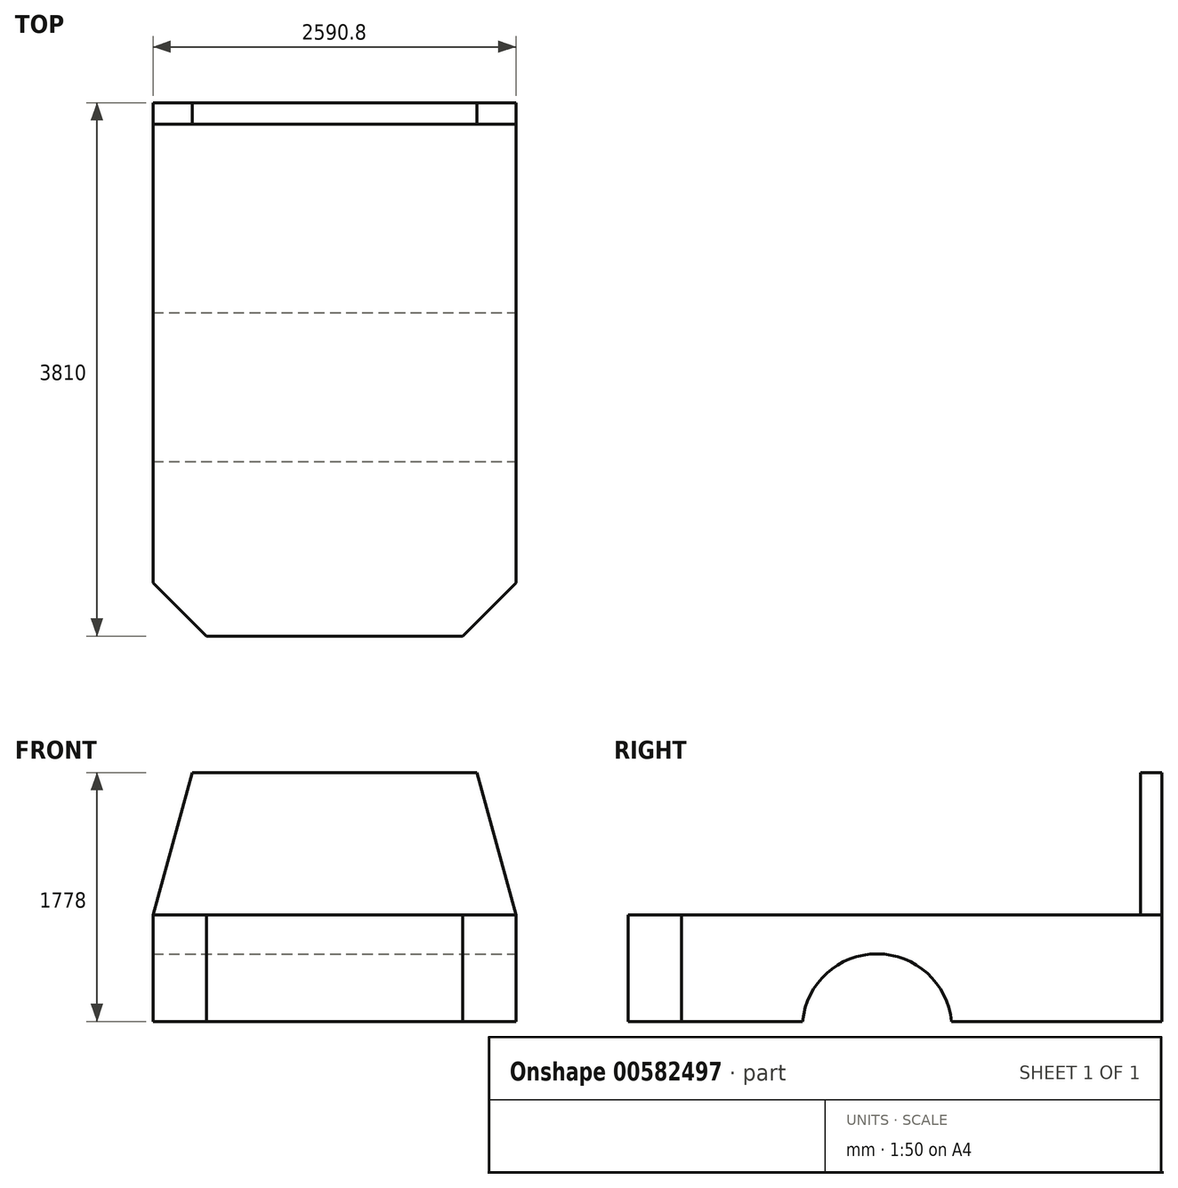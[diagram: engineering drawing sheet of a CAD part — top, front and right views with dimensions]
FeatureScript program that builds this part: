
annotation { "Feature Type Name" : "Feature", "Feature Type Description" : "" }
export const myFeature = defineFeature(function(context is Context, id is Id, definition is map)
    precondition{}
    {
        {
            assignVariable(context, id + "F0", {"name" : "Height", "anyValue" : 762 * mm});
        }
        {
            assignVariable(context, id + "F1", {"name" : "Length", "anyValue" : 3810 * mm});
        }
        {
            var Q0;
            Q0=qCreatedBy(makeId("Front.planeOp"),FACE);
            cPlane(context, id + "F2", {"entities" : qUnion([Q0]), "cplaneType" : CPlaneType.OFFSET, "offset" : getVariable(context, 'Length'), "width" : 150 * mm, "height" : 150 * mm});
        }
        {
            var Q0;
            Q0=qCreatedBy(makeId("Top.planeOp"),FACE);
            var sketch = newSketch(context, id + "F3", { "sketchPlane" : qUnion([Q0])});
            skLineSegment(sketch, "E0", {"start": v(2146.04, 0) * mm, "end": v(-1849.37, 0) * mm, "construction": true});
            skLineSegment(sketch, "E1", {"start": v(0, 0) * mm, "end": v(0, -5385.1) * mm, "construction": true});
            skLineSegment(sketch, "E2.bottom", {"start": v(-1295.4, 0) * mm, "end": v(1295.4, 0) * mm});
            skLineSegment(sketch, "E2.top", {"start": v(-1295.4, -3810) * mm, "end": v(1295.4, -3810) * mm});
            skLineSegment(sketch, "E2.left", {"start": v(-1295.4, 0) * mm, "end": v(-1295.4, -3810) * mm});
            skLineSegment(sketch, "E2.right", {"start": v(1295.4, 0) * mm, "end": v(1295.4, -3810) * mm});
            skSolve(sketch);
        }
        {
            var Q0;
            Q0=makeQuery(id+"F3.imprint","IMPRINT",FACE,{"disambiguationData":[TD([[makeQuery(id+"F3.imprint","IMPRINT",EDGE,{"derivedFrom":sQuery(id+"F3.wireOp",EDGE,"E2.bottom")}),-1.0]])]});
            extrude(context, id + "F4", {"entities" : qUnion([Q0]), "oppositeDirection" : true, "depth" : getVariable(context, 'Height'), "offsetDistance" : 25 * mm});
        }
        {
            var Q0;
            Q0=qCreatedBy(makeId("Right.planeOp"),FACE);
            var sketch = newSketch(context, id + "F5", { "sketchPlane" : qUnion([Q0])});
            skCircle(sketch, "E3", {"center": v(-2032, -812.8) * mm, "radius": 533.4 * mm});
            skLineSegment(sketch, "E4", {"start": v(0, -1232.81) * mm, "end": v(0, 1011) * mm, "construction": true});
            skLineSegment(sketch, "E5", {"start": v(-4610.37, 0) * mm, "end": v(0, 0) * mm, "construction": true});
            skSolve(sketch);
        }
        {
            var Q0;
            Q0=makeQuery(id+"F5.imprint","IMPRINT",FACE,{"disambiguationData":[TD([[makeQuery(id+"F5.imprint","IMPRINT",EDGE,{"derivedFrom":sQuery(id+"F5.wireOp",EDGE,"E3")}),1.0]])]});
            extrude(context, id + "F6", {"entities" : qUnion([Q0]), "operationType" : NewBodyOperationType.REMOVE, "endBound" : BoundingType.THROUGH_ALL, "oppositeDirection" : true, "depth" : 25 * mm, "offsetDistance" : 25 * mm, "hasSecondDirection" : true, "secondDirectionBound" : BoundingType.THROUGH_ALL, "secondDirectionOppositeDirection" : false, "secondDirectionDepth" : 25 * mm});
        }
        {
            var Q0;
            Q0=qCreatedBy(makeId("Top.planeOp"),FACE);
            var sketch = newSketch(context, id + "F7", { "sketchPlane" : qUnion([Q0])});
            skLineSegment(sketch, "E6", {"start": v(1295.4, 0) * mm, "end": v(1295.4, -3810) * mm});
            skLineSegment(sketch, "E7", {"start": v(1776.04, -3810) * mm, "end": v(-1595.7, -3810) * mm});
            skLineSegment(sketch, "E8", {"start": v(914.4, -3810) * mm, "end": v(1295.4, -3429) * mm});
            skLineSegment(sketch, "E9", {"start": v(-1295.4, 0) * mm, "end": v(-1295.4, -3810) * mm});
            skLineSegment(sketch, "E10.MirrorCS", {"start": v(-914.4, -3810) * mm, "end": v(-1295.4, -3429) * mm});
            skSolve(sketch);
        }
        {
            var Q0;
            {var subQ3=sQuery(id+"F7.wireOp",EDGE,"E8");Q0=makeQuery(id+"F7.imprint","IMPRINT",FACE,{"disambiguationData":[TD([[makeQuery(id+"F7.imprint","IMPRINT",EDGE,{"derivedFrom":subQ3}),-1.0]])]});}
            var Q1;
            {var subQ3=sQuery(id+"F7.wireOp",EDGE,"E10.MirrorCS");Q1=makeQuery(id+"F7.imprint","IMPRINT",FACE,{"disambiguationData":[TD([[makeQuery(id+"F7.imprint","IMPRINT",EDGE,{"derivedFrom":subQ3}),1.0]])]});}
            extrude(context, id + "F8", {"entities" : qUnion([Q0, Q1]), "operationType" : NewBodyOperationType.REMOVE, "endBound" : BoundingType.THROUGH_ALL, "oppositeDirection" : true, "depth" : 25 * mm, "offsetDistance" : 25 * mm});
        }
        {
            var Q0;
            Q0=qCreatedBy(makeId("Front.planeOp"),FACE);
            var sketch = newSketch(context, id + "F9", { "sketchPlane" : qUnion([Q0])});
            skLineSegment(sketch, "E11", {"start": v(-1295.4, 0) * mm, "end": v(1295.4, 0) * mm});
            skLineSegment(sketch, "E12", {"start": v(-1295.4, 0) * mm, "end": v(-1295.4, -762) * mm});
            skLineSegment(sketch, "E13", {"start": v(1295.4, 0) * mm, "end": v(1295.4, -762) * mm});
            skLineSegment(sketch, "E14", {"start": v(1295.4, 0) * mm, "end": v(1016, 1016) * mm});
            skLineSegment(sketch, "E15.MirrorCS", {"start": v(-1295.4, 0) * mm, "end": v(-1016, 1016) * mm});
            skLineSegment(sketch, "E16", {"start": v(1016, 1016) * mm, "end": v(-1016, 1016) * mm});
            skSolve(sketch);
        }
        {
            var Q0;
            Q0=makeQuery(id+"F9.imprint","IMPRINT",FACE,{"disambiguationData":[TD([[makeQuery(id+"F9.imprint","IMPRINT",EDGE,{"derivedFrom":sQuery(id+"F9.wireOp",EDGE,"E11")}),1.0]])]});
            extrude(context, id + "F10", {"entities" : qUnion([Q0]), "operationType" : NewBodyOperationType.ADD, "depth" : 152.4 * mm, "offsetDistance" : 25 * mm});
        }
    });
